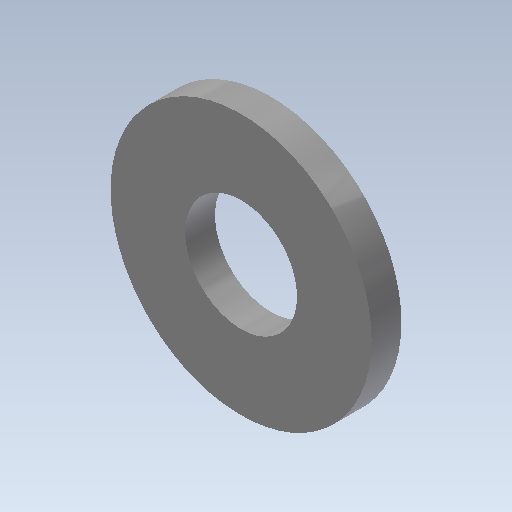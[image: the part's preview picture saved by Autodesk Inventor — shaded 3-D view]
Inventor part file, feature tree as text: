
AUTODESK INVENTOR PART (.ipt)
format: ipt  version: 2020 (Build 240168000, 168)  size: 88,064 bytes
history: native  units: in
note: dims shown in document units (in); Inventor stores cm internally (conversion verified against a paired STEP export)
features: extrude x1, sketch x1
ambient origin geometry x8: Origin, YZ Plane, XZ Plane, XY Plane, X Axis, Y Axis, Z Axis, Center Point
bodies: Solid1 (feature_tree)
feature tree (2):
  extrude  "Extrusion1"  Depth=0.05in
  sketch  "Sketch1"  dims[d0=0.1875in d1=0.4375in d2=0.05in d3=0.0in]
